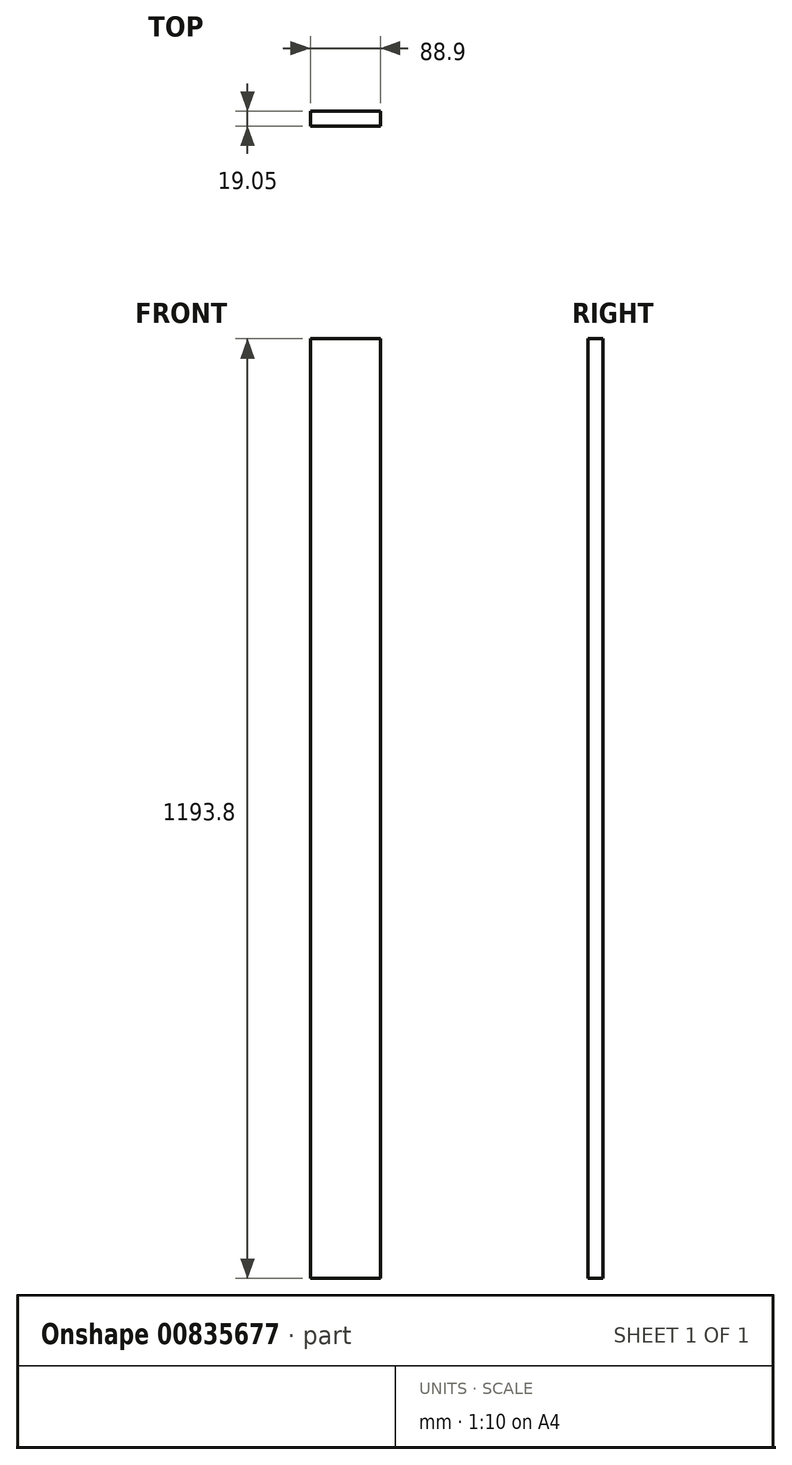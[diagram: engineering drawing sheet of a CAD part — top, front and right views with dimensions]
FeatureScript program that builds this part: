
annotation { "Feature Type Name" : "Feature", "Feature Type Description" : "" }
export const myFeature = defineFeature(function(context is Context, id is Id, definition is map)
    precondition{}
    {
        {
            var Q0;
            Q0=qCreatedBy(makeId("Front.planeOp"),FACE);
            var sketch = newSketch(context, id + "F0", { "sketchPlane" : qUnion([Q0])});
            skLineSegment(sketch, "E0.bottom", {"start": v(0, 0) * mm, "end": v(88.9, 0) * mm});
            skLineSegment(sketch, "E0.top", {"start": v(0, 1193.8) * mm, "end": v(88.9, 1193.8) * mm});
            skLineSegment(sketch, "E0.left", {"start": v(0, 0) * mm, "end": v(0, 1193.8) * mm});
            skLineSegment(sketch, "E0.right", {"start": v(88.9, 0) * mm, "end": v(88.9, 1193.8) * mm});
            skSolve(sketch);
        }
        {
            var Q0;
            Q0 = qSketchRegion(id + "F0", true);
            extrude(context, id + "F1", {"entities" : qUnion([Q0]), "depth" : 19.05 * mm, "offsetDistance" : 25.4 * mm});
        }
    });
